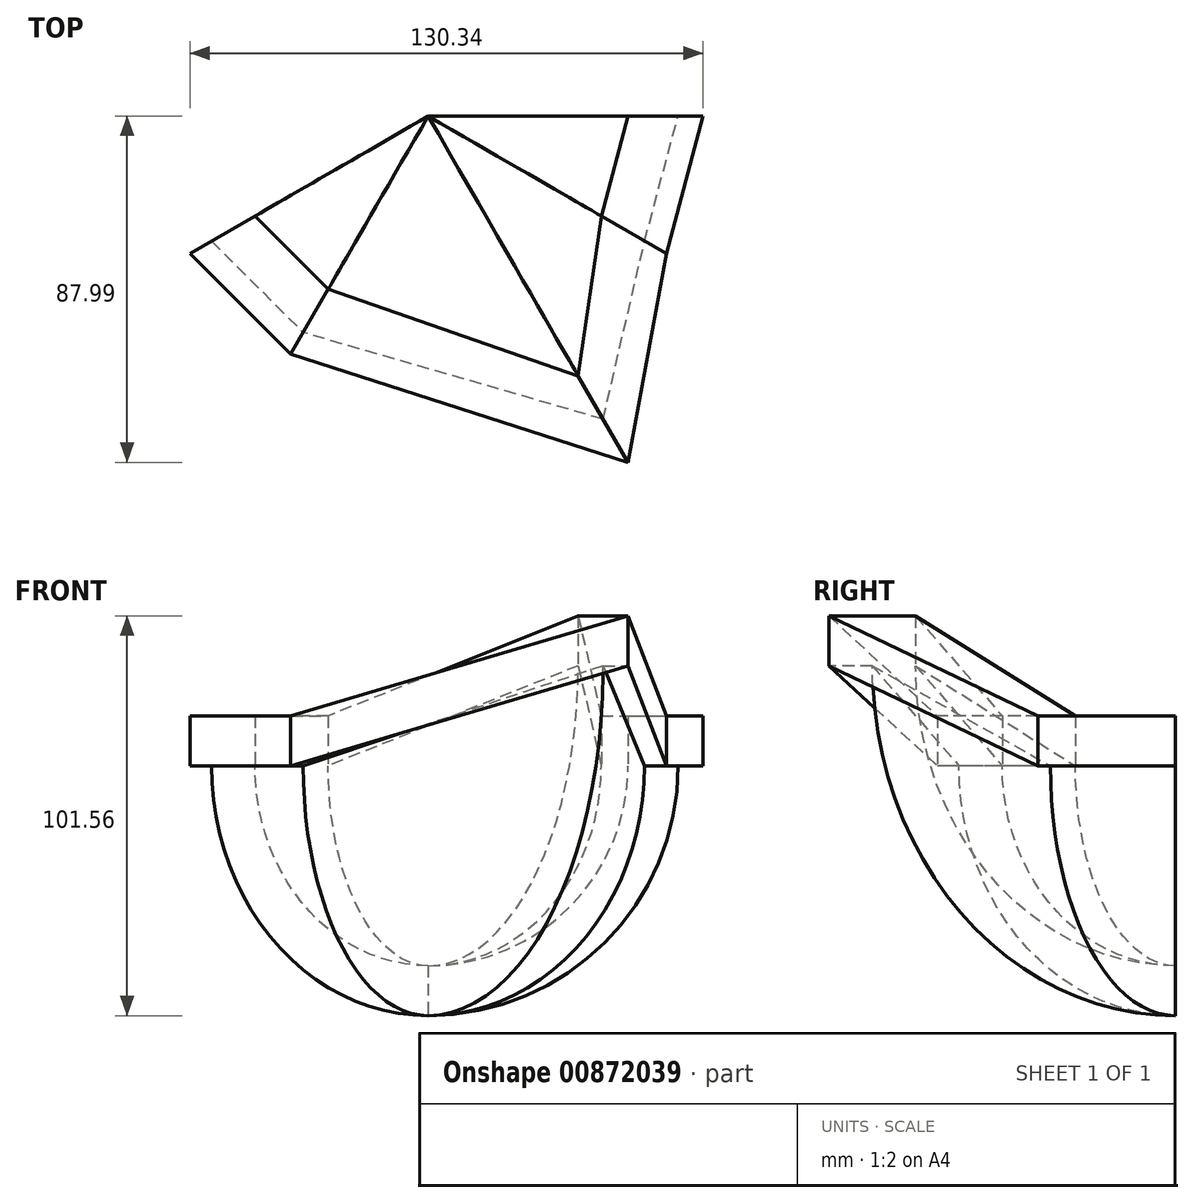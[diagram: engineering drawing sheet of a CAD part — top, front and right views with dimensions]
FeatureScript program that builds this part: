
annotation { "Feature Type Name" : "Feature", "Feature Type Description" : "" }
export const myFeature = defineFeature(function(context is Context, id is Id, definition is map)
    precondition{}
    {
        {
            var Q0;
            Q0=qCreatedBy(makeId("Front.planeOp"),FACE);
            var sketch = newSketch(context, id + "F0", { "sketchPlane" : qUnion([Q0])});
            skArc(sketch, "E0", {"start": v(0, -63.5) * mm, "mid": v(44.9, -44.9) * mm, "end": v(63.5, 0) * mm});
            skArc(sketch, "E1", {"start": v(0, -50.8) * mm, "mid": v(35.92, -35.92) * mm, "end": v(50.8, 0) * mm});
            skLineSegment(sketch, "E2.right", {"start": v(0, -50.8) * mm, "end": v(0, -63.5) * mm});
            skLineSegment(sketch, "E3.bottom", {"start": v(50.8, 12.66) * mm, "end": v(69.85, 12.66) * mm});
            skLineSegment(sketch, "E3.top", {"start": v(63.5, 0) * mm, "end": v(69.85, 0) * mm});
            skLineSegment(sketch, "E3.left", {"start": v(50.8, 12.66) * mm, "end": v(50.8, 0) * mm});
            skLineSegment(sketch, "E3.right", {"start": v(69.85, 12.66) * mm, "end": v(69.85, 0) * mm});
            skLineSegment(sketch, "E4", {"start": v(0, 0) * mm, "end": v(0, -63.5) * mm});
            skSolve(sketch);
        }
        {
            var Q0;
            Q0=sQuery(id+"F0.wireOp",EDGE,"E4");
            cPlane(context, id + "F1", {"entities" : qUnion([Q0]), "cplaneType" : CPlaneType.LINE_ANGLE, "offset" : 25.4 * mm, "angle" : 30 * degree, "oppositeDirection" : true, "width" : 152.4 * mm, "height" : 152.4 * mm});
        }
        {
            var Q0;
            Q0=qCreatedBy(id+"F1.planeOp",FACE);
            var sketch = newSketch(context, id + "F2", { "sketchPlane" : qUnion([Q0])});
            skArc(sketch, "E5", {"start": v(0, -63.5) * mm, "mid": v(62.86, -37.46) * mm, "end": v(88.9, 25.4) * mm});
            skArc(sketch, "E6", {"start": v(0, -50.8) * mm, "mid": v(53.88, -28.48) * mm, "end": v(76.2, 25.4) * mm});
            skLineSegment(sketch, "E7.right", {"start": v(0, -50.8) * mm, "end": v(0, -63.5) * mm});
            skLineSegment(sketch, "E8.bottom", {"start": v(76.2, 38.06) * mm, "end": v(101.6, 38.06) * mm});
            skLineSegment(sketch, "E8.top", {"start": v(88.9, 25.4) * mm, "end": v(101.6, 25.4) * mm});
            skLineSegment(sketch, "E8.left", {"start": v(76.2, 38.06) * mm, "end": v(76.2, 25.4) * mm});
            skLineSegment(sketch, "E8.right", {"start": v(101.6, 38.06) * mm, "end": v(101.6, 25.4) * mm});
            skLineSegment(sketch, "E9", {"start": v(0, 25.4) * mm, "end": v(0, -63.5) * mm});
            skSolve(sketch);
        }
        {
            var Q0;
            Q0=sQuery(id+"F2.wireOp",EDGE,"E9");
            cPlane(context, id + "F3", {"entities" : qUnion([Q0]), "cplaneType" : CPlaneType.LINE_ANGLE, "offset" : 25.4 * mm, "angle" : 30 * degree, "width" : 152.4 * mm, "height" : 152.4 * mm});
        }
        {
            var Q0;
            Q0=qCreatedBy(id+"F3.planeOp",FACE);
            var sketch = newSketch(context, id + "F4", { "sketchPlane" : qUnion([Q0])});
            skArc(sketch, "E10", {"start": v(0, -63.5) * mm, "mid": v(44.9, -44.9) * mm, "end": v(63.5, 0) * mm});
            skArc(sketch, "E11", {"start": v(0, -50.8) * mm, "mid": v(35.92, -35.92) * mm, "end": v(50.8, 0) * mm});
            skLineSegment(sketch, "E12.right", {"start": v(0, -50.8) * mm, "end": v(0, -63.5) * mm});
            skLineSegment(sketch, "E13.bottom", {"start": v(50.8, 12.66) * mm, "end": v(69.85, 12.66) * mm});
            skLineSegment(sketch, "E13.top", {"start": v(63.5, 0) * mm, "end": v(69.85, 0) * mm});
            skLineSegment(sketch, "E13.left", {"start": v(50.8, 12.66) * mm, "end": v(50.8, 0) * mm});
            skLineSegment(sketch, "E13.right", {"start": v(69.85, 12.66) * mm, "end": v(69.85, 0) * mm});
            skLineSegment(sketch, "E14", {"start": v(0, 0) * mm, "end": v(0, -63.5) * mm});
            skSolve(sketch);
        }
        {
            var Q0;
            Q0=sQuery(id+"F0.wireOp",EDGE,"E4");
            cPlane(context, id + "F5", {"entities" : qUnion([Q0]), "cplaneType" : CPlaneType.LINE_ANGLE, "offset" : 1524 * mm, "angle" : 60 * degree, "width" : 152.4 * mm, "height" : 152.4 * mm});
        }
        {
            var Q0;
            Q0=qCreatedBy(id+"F5.planeOp",FACE);
            var sketch = newSketch(context, id + "F6", { "sketchPlane" : qUnion([Q0])});
            skArc(sketch, "E15", {"start": v(0, -63.5) * mm, "mid": v(44.9, -44.9) * mm, "end": v(63.5, 0) * mm});
            skArc(sketch, "E16", {"start": v(0, -50.8) * mm, "mid": v(35.92, -35.92) * mm, "end": v(50.8, 0) * mm});
            skLineSegment(sketch, "E17.right", {"start": v(0, -50.8) * mm, "end": v(0, -63.5) * mm});
            skLineSegment(sketch, "E18.bottom", {"start": v(50.8, 12.66) * mm, "end": v(69.85, 12.66) * mm});
            skLineSegment(sketch, "E18.top", {"start": v(63.5, 0) * mm, "end": v(69.85, 0) * mm});
            skLineSegment(sketch, "E18.left", {"start": v(50.8, 12.66) * mm, "end": v(50.8, 0) * mm});
            skLineSegment(sketch, "E18.right", {"start": v(69.85, 12.66) * mm, "end": v(69.85, 0) * mm});
            skLineSegment(sketch, "E19", {"start": v(0, 0) * mm, "end": v(0, -63.5) * mm});
            skSolve(sketch);
        }
        {
            var Q0;
            Q0=sQuery(id+"F0.wireOp",EDGE,"E4");
            cPlane(context, id + "F7", {"entities" : qUnion([Q0]), "cplaneType" : CPlaneType.LINE_ANGLE, "offset" : 25.4 * mm, "angle" : 60 * degree, "oppositeDirection" : true, "width" : 152.4 * mm, "height" : 152.4 * mm});
        }
        {
            var Q0;
            Q0=qCreatedBy(id+"F7.planeOp",FACE);
            var sketch = newSketch(context, id + "F8", { "sketchPlane" : qUnion([Q0])});
            skArc(sketch, "E20", {"start": v(0, -63.5) * mm, "mid": v(44.9, -44.9) * mm, "end": v(63.5, 0) * mm});
            skArc(sketch, "E21", {"start": v(0, -50.8) * mm, "mid": v(35.92, -35.92) * mm, "end": v(50.8, 0) * mm});
            skLineSegment(sketch, "E22.right", {"start": v(0, -50.8) * mm, "end": v(0, -63.5) * mm});
            skLineSegment(sketch, "E23.bottom", {"start": v(50.8, 12.66) * mm, "end": v(69.85, 12.66) * mm});
            skLineSegment(sketch, "E23.top", {"start": v(63.5, 0) * mm, "end": v(69.85, 0) * mm});
            skLineSegment(sketch, "E23.left", {"start": v(50.8, 12.66) * mm, "end": v(50.8, 0) * mm});
            skLineSegment(sketch, "E23.right", {"start": v(69.85, 12.66) * mm, "end": v(69.85, 0) * mm});
            skLineSegment(sketch, "E24", {"start": v(0, 0) * mm, "end": v(0, -63.5) * mm});
            skSolve(sketch);
        }
        {
            var Q0;
            {var subQ1=sQuery(id+"F2.wireOp",EDGE,"E5");Q0=makeQuery(id+"F2.imprint","IMPRINT",FACE,{"disambiguationData":[TD([[makeQuery(id+"F2.imprint","IMPRINT",EDGE,{"derivedFrom":subQ1}),1.0]])]});}
            var Q1;
            {var subQ1=sQuery(id+"F8.wireOp",EDGE,"E20");Q1=makeQuery(id+"F8.imprint","IMPRINT",FACE,{"disambiguationData":[TD([[makeQuery(id+"F8.imprint","IMPRINT",EDGE,{"derivedFrom":subQ1}),1.0]])]});}
            loft(context, id + "F9", {"sheetProfilesArray" : [{ "sheetProfileEntities" : qUnion([Q0]) }, { "sheetProfileEntities" : qUnion([Q1]) }]});
        }
        {
            var Q1;
            {var subQ1=sQuery(id+"F2.wireOp",EDGE,"E5");Q1=makeQuery(id+"F9.opLoft","CAP_FACE",FACE,{"disambiguationData":[OSD([makeQuery(id+"F2.imprint","IMPRINT",FACE,{"disambiguationData":[TD([[makeQuery(id+"F2.imprint","IMPRINT",EDGE,{"derivedFrom":subQ1}),1.0]])]})])],"isStart":true});}
            var Q2;
            {var subQ1=sQuery(id+"F4.wireOp",EDGE,"E10");Q2=makeQuery(id+"F4.imprint","IMPRINT",FACE,{"disambiguationData":[TD([[makeQuery(id+"F4.imprint","IMPRINT",EDGE,{"derivedFrom":subQ1}),1.0]])]});}
            loft(context, id + "F10", {"operationType" : NewBodyOperationType.ADD, "sheetProfilesArray" : [{ "sheetProfileEntities" : qUnion([Q1]) }, { "sheetProfileEntities" : qUnion([Q2]) }]});
        }
        {
            var Q1;
            {var subQ1=sQuery(id+"F8.wireOp",EDGE,"E20");Q1=makeQuery(id+"F9.opLoft","CAP_FACE",FACE,{"disambiguationData":[OSD([makeQuery(id+"F8.imprint","IMPRINT",FACE,{"disambiguationData":[TD([[makeQuery(id+"F8.imprint","IMPRINT",EDGE,{"derivedFrom":subQ1}),1.0]])]})])],"isStart":true});}
            var Q2;
            {var subQ1=sQuery(id+"F0.wireOp",EDGE,"E0");Q2=makeQuery(id+"F0.imprint","IMPRINT",FACE,{"disambiguationData":[TD([[makeQuery(id+"F0.imprint","IMPRINT",EDGE,{"derivedFrom":subQ1}),1.0]])]});}
            loft(context, id + "F11", {"operationType" : NewBodyOperationType.ADD, "sheetProfilesArray" : [{ "sheetProfileEntities" : qUnion([Q1]) }, { "sheetProfileEntities" : qUnion([Q2]) }]});
        }
        {
            var Q1;
            {var subQ1=sQuery(id+"F6.wireOp",EDGE,"E15");Q1=makeQuery(id+"F6.imprint","IMPRINT",FACE,{"disambiguationData":[TD([[makeQuery(id+"F6.imprint","IMPRINT",EDGE,{"derivedFrom":subQ1}),1.0]])]});}
            var Q2;
            {var subQ1=sQuery(id+"F4.wireOp",EDGE,"E10");Q2=makeQuery(id+"F10.opLoft","CAP_FACE",FACE,{"disambiguationData":[OSD([makeQuery(id+"F4.imprint","IMPRINT",FACE,{"disambiguationData":[TD([[makeQuery(id+"F4.imprint","IMPRINT",EDGE,{"derivedFrom":subQ1}),1.0]])]})])],"isStart":true});}
            loft(context, id + "F12", {"operationType" : NewBodyOperationType.ADD, "sheetProfilesArray" : [{ "sheetProfileEntities" : qUnion([Q1]) }, { "sheetProfileEntities" : qUnion([Q2]) }]});
        }
    });
